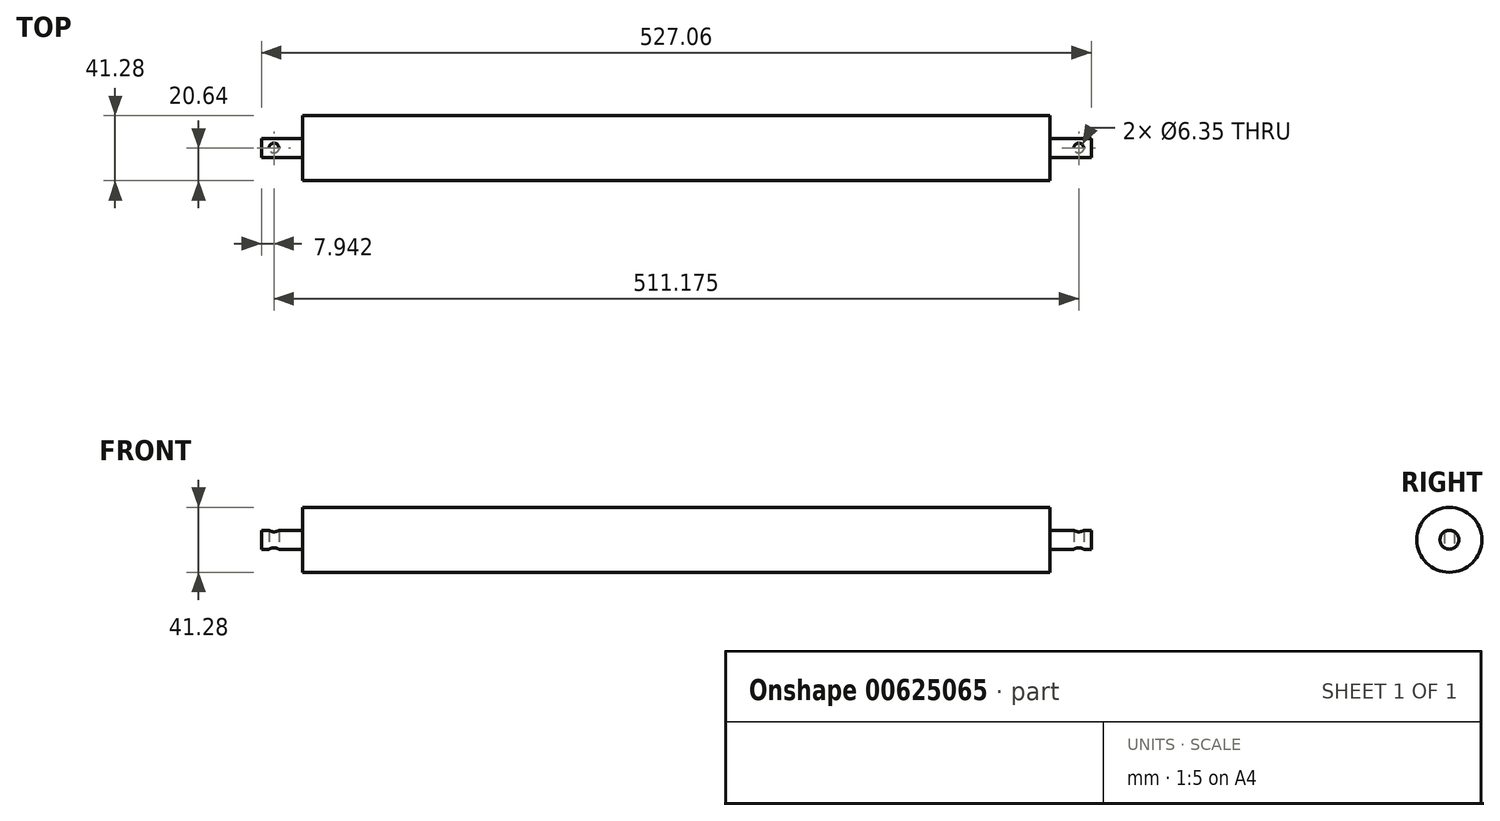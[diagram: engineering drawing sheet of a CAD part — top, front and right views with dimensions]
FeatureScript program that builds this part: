
annotation { "Feature Type Name" : "Feature", "Feature Type Description" : "" }
export const myFeature = defineFeature(function(context is Context, id is Id, definition is map)
    precondition{}
    {
        {
            var Q0;
            Q0=qCreatedBy(makeId("Right.planeOp"),FACE);
            var sketch = newSketch(context, id + "F0", { "sketchPlane" : qUnion([Q0])});
            skCircle(sketch, "E0", {"center": v(0, 0) * mm, "radius": 20.64 * mm});
            skCircle(sketch, "E1", {"center": v(0, 0) * mm, "radius": 6 * mm});
            skSolve(sketch);
        }
        {
            var Q0;
            Q0=makeQuery(id+"F0.imprint","IMPRINT",FACE,{"disambiguationData":[TD([[makeQuery(id+"F0.imprint","IMPRINT",EDGE,{"derivedFrom":sQuery(id+"F0.wireOp",EDGE,"E0")}),1.0]])]});
            extrude(context, id + "F1", {"entities" : qUnion([Q0]), "endBound" : BoundingType.SYMMETRIC, "depth" : 474.66 * mm, "offsetDistance" : 25.4 * mm});
        }
        {
            var Q0;
            Q0=makeQuery(id+"F0.imprint","IMPRINT",FACE,{"disambiguationData":[TD([[makeQuery(id+"F0.imprint","IMPRINT",EDGE,{"derivedFrom":sQuery(id+"F0.wireOp",EDGE,"E1")}),1.0]])]});
            extrude(context, id + "F2", {"entities" : qUnion([Q0]), "operationType" : NewBodyOperationType.ADD, "endBound" : BoundingType.SYMMETRIC, "depth" : 527.05 * mm, "offsetDistance" : 25.4 * mm});
        }
        {
            var Q0;
            Q0=qCreatedBy(makeId("Top.planeOp"),FACE);
            var sketch = newSketch(context, id + "F3", { "sketchPlane" : qUnion([Q0])});
            skCircle(sketch, "E2", {"center": v(255.59, 0) * mm, "radius": 3.18 * mm});
            skCircle(sketch, "E3", {"center": v(-255.59, 0) * mm, "radius": 3.18 * mm});
            skSolve(sketch);
        }
        {
            var Q0;
            Q0=qSketchRegion(id+"F3",true);
            var Q1;
            Q1=sQuery(id+"F3.wireOp",EDGE,"E3");
            var Q2;
            Q2=sQuery(id+"F3.wireOp",EDGE,"E2");
            extrude(context, id + "F4", {"entities" : qUnion([Q0]), "operationType" : NewBodyOperationType.REMOVE, "surfaceEntities" : qUnion([Q1, Q2]), "endBound" : BoundingType.SYMMETRIC, "depth" : 12.7 * mm, "offsetDistance" : 25.4 * mm});
        }
    });
